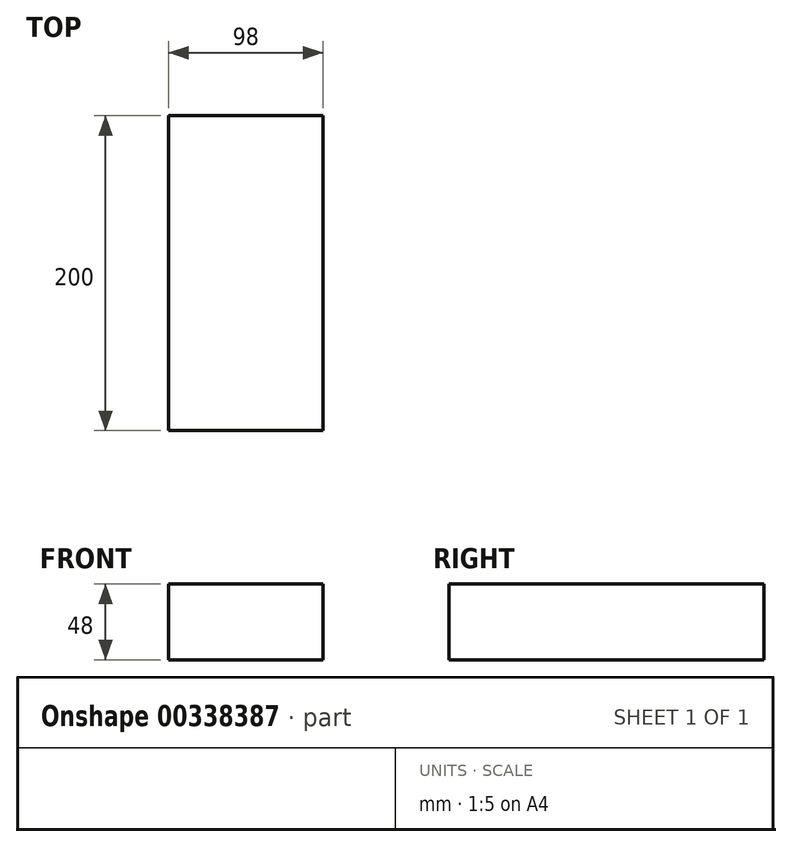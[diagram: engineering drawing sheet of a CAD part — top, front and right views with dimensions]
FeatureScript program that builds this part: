
annotation { "Feature Type Name" : "Feature", "Feature Type Description" : "" }
export const myFeature = defineFeature(function(context is Context, id is Id, definition is map)
    precondition{}
    {
        {
            var Q0;
            Q0=qCreatedBy(makeId("Front.planeOp"),FACE);
            var sketch = newSketch(context, id + "F0", { "sketchPlane" : qUnion([Q0])});
            skLineSegment(sketch, "E0.bottom", {"start": v(-49, -24) * mm, "end": v(49, -24) * mm});
            skLineSegment(sketch, "E0.top", {"start": v(-49, 24) * mm, "end": v(49, 24) * mm});
            skLineSegment(sketch, "E0.left", {"start": v(-49, -24) * mm, "end": v(-49, 24) * mm});
            skLineSegment(sketch, "E0.right", {"start": v(49, -24) * mm, "end": v(49, 24) * mm});
            skPoint(sketch, "E0.middle", {"position": v(0, 0) * mm});
            skSolve(sketch);
        }
        {
            var Q0;
            Q0=makeQuery(id+"F0.imprint","IMPRINT",FACE,{"disambiguationData":[TD([[makeQuery(id+"F0.imprint","IMPRINT",EDGE,{"derivedFrom":sQuery(id+"F0.wireOp",EDGE,"E0.bottom")}),1.0]])]});
            extrude(context, id + "F1", {"entities" : qUnion([Q0]), "offsetDistance" : 25 * mm, "depth" : 200 * mm});
        }
    });
